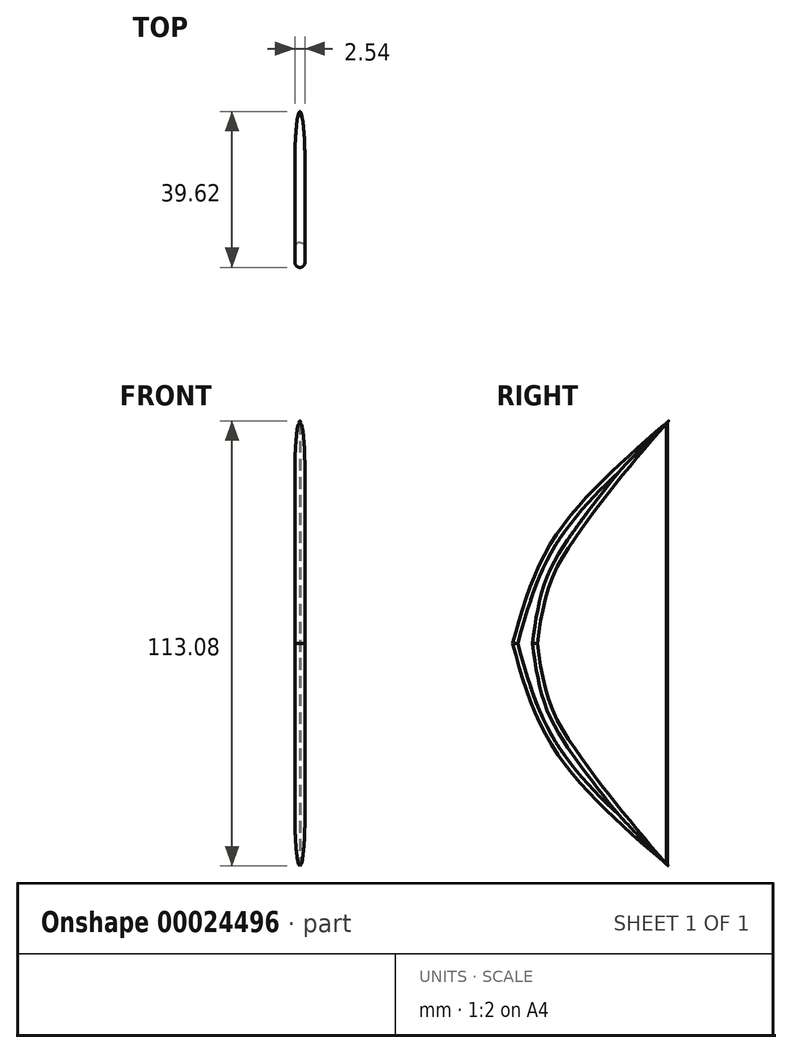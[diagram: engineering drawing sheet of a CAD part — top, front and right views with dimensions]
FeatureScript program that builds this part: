
annotation { "Feature Type Name" : "Feature", "Feature Type Description" : "" }
export const myFeature = defineFeature(function(context is Context, id is Id, definition is map)
    precondition{}
    {
        {
            var Q0;
            Q0=qCreatedBy(makeId("Right.planeOp"),FACE);
            var sketch = newSketch(context, id + "F0", { "sketchPlane" : qUnion([Q0])});
            skLineSegment(sketch, "E0", {"start": v(0, 0) * mm, "end": v(6.35, 0) * mm});
            skFitSpline(sketch, "E1", {"points": [v(0, 0) * mm, v(10.67, 26.97) * mm, v(39.62, 56.54) * mm], "startDerivative": vector(16.62, 60.3) * mm, "endDerivative": vector(61.3, 53) * mm});
            skFitSpline(sketch, "E2", {"points": [v(6.35, 0) * mm, v(14.94, 25.45) * mm, v(39.62, 56.54) * mm], "startDerivative": vector(10.47, 88.13) * mm, "endDerivative": vector(46.66, 52.57) * mm});
            skSolve(sketch);
        }
        {
            var Q0;
            Q0 = qSketchRegion(id + "F0", true);
            extrude(context, id + "F1", {"entities" : qUnion([Q0]), "depth" : 2.54 * mm});
        }
        {
            var Q0;
            Q0=makeQuery(id+"F1.opExtrude","SWEPT_BODY",BODY,{"disambiguationData":[OSD([sQuery(id+"F0.wireOp",EDGE,"E0"),sQuery(id+"F0.wireOp",EDGE,"E1"),sQuery(id+"F0.wireOp",EDGE,"E2")])]});
            var Q1;
            Q1=makeQuery(id+"F1.opExtrude","SWEPT_FACE",FACE,{"disambiguationData":[OSD([sQuery(id+"F0.wireOp",EDGE,"E0")])]});
            mirror(context, id + "F2", {"operationType" : NewBodyOperationType.ADD, "entities" : qUnion([Q0]), "mirrorPlane" : qUnion([Q1])});
        }
        {
            var Q0;
            Q0=qCreatedBy(makeId("Top.planeOp"),FACE);
            var sketch = newSketch(context, id + "F3", { "sketchPlane" : qUnion([Q0])});
            skCircle(sketch, "E3", {"center": v(1.25, 39.23) * mm, "radius": 0.13 * mm});
            skLineSegment(sketch, "E4", {"start": v(-0.01, 39.63) * mm, "end": v(2.52, 39.63) * mm});
            skLineSegment(sketch, "E5", {"start": v(1.25, 39.63) * mm, "end": v(1.25, 38.36) * mm});
            skSolve(sketch);
        }
        {
            var Q0;
            Q0 = qSketchRegion(id + "F3", true);
            extrude(context, id + "F4", {"entities" : qUnion([Q0]), "depth" : 58.42 * mm});
        }
        {
            var Q0;
            {var subQ0=makeQuery(id+"F1.opExtrude","CAP_FACE",FACE,{"disambiguationData":[OSD([sQuery(id+"F0.wireOp",EDGE,"E0"),sQuery(id+"F0.wireOp",EDGE,"E1"),sQuery(id+"F0.wireOp",EDGE,"E2")])],"isStart":false});Q0=makeQuery(id+"F2.boolean.opBoolean","MERGE",FACE,{"derivedFrom":[subQ0,makeQuery(id+"F2.opPattern","COPY",FACE,{"derivedFrom":subQ0,"instanceName":"1"})]});}
            var Q1;
            {var subQ0=makeQuery(id+"F1.opExtrude","CAP_FACE",FACE,{"disambiguationData":[OSD([sQuery(id+"F0.wireOp",EDGE,"E0"),sQuery(id+"F0.wireOp",EDGE,"E1"),sQuery(id+"F0.wireOp",EDGE,"E2")])],"isStart":true});Q1=makeQuery(id+"F2.boolean.opBoolean","MERGE",FACE,{"derivedFrom":[subQ0,makeQuery(id+"F2.opPattern","COPY",FACE,{"derivedFrom":subQ0,"instanceName":"1"})]});}
            fillet(context, id + "F5", {"entities" : qUnion([Q0, Q1]), "radius" : 1.27 * mm, "tangentPropagation" : true, "allowEdgeOverflow" : false});
        }
        {
            var Q0;
            Q0=qCreatedBy(makeId("Right.planeOp"),FACE);
            var sketch = newSketch(context, id + "F6", { "sketchPlane" : qUnion([Q0])});
            skLineSegment(sketch, "E6", {"start": v(38.62, 55.54) * mm, "end": v(39.52, 56.44) * mm});
            skLineSegment(sketch, "E7", {"start": v(38.56, 58.76) * mm, "end": v(38.62, 55.54) * mm});
            skLineSegment(sketch, "E8", {"start": v(39.52, 56.44) * mm, "end": v(39.52, 58.79) * mm});
            skLineSegment(sketch, "E9", {"start": v(38.56, 58.76) * mm, "end": v(39.52, 58.79) * mm});
            skSolve(sketch);
        }
        {
            var Q0;
            Q0 = qSketchRegion(id + "F6", true);
            extrude(context, id + "F7", {"entities" : qUnion([Q0]), "operationType" : NewBodyOperationType.REMOVE, "depth" : 25.4 * mm});
        }
        {
            var Q0;
            Q0=makeQuery(id+"F4.opExtrude","SWEPT_BODY",BODY,{"disambiguationData":[OSD([sQuery(id+"F3.wireOp",EDGE,"E3")])]});
            var Q1;
            Q1=makeQuery(id+"F4.opExtrude","CAP_FACE",FACE,{"disambiguationData":[OSD([sQuery(id+"F3.wireOp",EDGE,"E3")])],"isStart":true});
            mirror(context, id + "F8", {"operationType" : NewBodyOperationType.ADD, "entities" : qUnion([Q0]), "mirrorPlane" : qUnion([Q1])});
        }
    });
